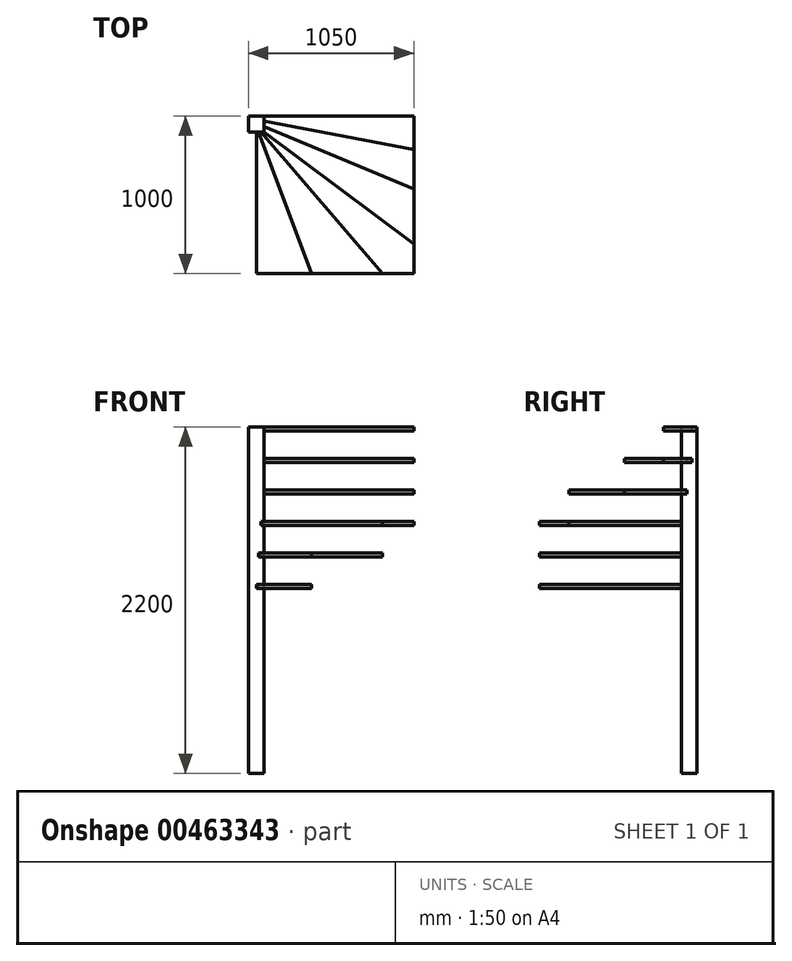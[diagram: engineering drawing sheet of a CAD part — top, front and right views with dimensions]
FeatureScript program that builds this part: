
annotation { "Feature Type Name" : "Feature", "Feature Type Description" : "" }
export const myFeature = defineFeature(function(context is Context, id is Id, definition is map)
    precondition{}
    {
        {
            var Q0;
            Q0=qCreatedBy(makeId("Top.planeOp"),FACE);
            var sketch = newSketch(context, id + "F0", { "sketchPlane" : qUnion([Q0])});
            skLineSegment(sketch, "E0.bottom", {"start": v(-50, 50) * mm, "end": v(50, 50) * mm});
            skLineSegment(sketch, "E0.top", {"start": v(-50, -50) * mm, "end": v(50, -50) * mm});
            skLineSegment(sketch, "E0.left", {"start": v(-50, 50) * mm, "end": v(-50, -50) * mm});
            skLineSegment(sketch, "E0.right", {"start": v(50, 50) * mm, "end": v(50, -50) * mm});
            skPoint(sketch, "E0.middle", {"position": v(0, 0) * mm});
            skSolve(sketch);
        }
        {
            var Q0;
            Q0=makeQuery(id+"F0.imprint","IMPRINT",FACE,{"disambiguationData":[TD([[makeQuery(id+"F0.imprint","IMPRINT",EDGE,{"derivedFrom":sQuery(id+"F0.wireOp",EDGE,"E0.bottom")}),-1.0]])]});
            extrude(context, id + "F1", {"entities" : qUnion([Q0]), "oppositeDirection" : true, "depth" : 2200 * mm, "offsetDistance" : 25 * mm});
        }
        {
            var Q0;
            Q0=makeQuery(id+"F1.opExtrude","CAP_FACE",FACE,{"disambiguationData":[OSD([sQuery(id+"F0.wireOp",EDGE,"E0.bottom"),sQuery(id+"F0.wireOp",EDGE,"E0.top"),sQuery(id+"F0.wireOp",EDGE,"E0.left"),sQuery(id+"F0.wireOp",EDGE,"E0.right")])],"isStart":true});
            var sketch = newSketch(context, id + "F2", { "sketchPlane" : qUnion([Q0])});
            skLineSegment(sketch, "E1", {"start": v(50, 50) * mm, "end": v(1000, 50) * mm});
            skLineSegment(sketch, "E2", {"start": v(1000, 50) * mm, "end": v(1000, -163.05) * mm});
            skLineSegment(sketch, "E3", {"start": v(1000, -163.05) * mm, "end": v(50, 17) * mm});
            skLineSegment(sketch, "E4", {"start": v(50, 17) * mm, "end": v(50, 50) * mm});
            skSolve(sketch);
        }
        {
            var Q0;
            Q0=makeQuery(id+"F2.imprint","IMPRINT",FACE,{"disambiguationData":[TD([[makeQuery(id+"F2.imprint","IMPRINT",EDGE,{"derivedFrom":sQuery(id+"F2.wireOp",EDGE,"E1")}),-1.0]])]});
            extrude(context, id + "F3", {"entities" : qUnion([Q0]), "oppositeDirection" : true, "depth" : 25 * mm, "offsetDistance" : 25 * mm});
        }
        {
            var Q0;
            Q0=qCreatedBy(makeId("Top.planeOp"),FACE);
            var sketch = newSketch(context, id + "F4", { "sketchPlane" : qUnion([Q0])});
            skLineSegment(sketch, "E5.0", {"start": v(50, 50) * mm, "end": v(1000, 50) * mm});
            skLineSegment(sketch, "E6.0", {"start": v(1000, 50) * mm, "end": v(1000, -163.05) * mm});
            skLineSegment(sketch, "E7.bottom", {"start": v(1000, 50) * mm, "end": v(-1000, 50) * mm});
            skLineSegment(sketch, "E7.top", {"start": v(1000, -950) * mm, "end": v(-1000, -950) * mm});
            skLineSegment(sketch, "E7.left", {"start": v(1000, 50) * mm, "end": v(1000, -950) * mm});
            skLineSegment(sketch, "E7.right", {"start": v(-1000, 50) * mm, "end": v(-1000, -950) * mm});
            skSolve(sketch);
        }
        {
            var Q0;
            Q0=makeQuery(id+"F1.opExtrude","CAP_FACE",FACE,{"disambiguationData":[OSD([sQuery(id+"F0.wireOp",EDGE,"E0.bottom"),sQuery(id+"F0.wireOp",EDGE,"E0.top"),sQuery(id+"F0.wireOp",EDGE,"E0.left"),sQuery(id+"F0.wireOp",EDGE,"E0.right")])],"isStart":true});
            cPlane(context, id + "F5", {"entities" : qUnion([Q0]), "cplaneType" : CPlaneType.OFFSET, "offset" : 200 * mm, "oppositeDirection" : true, "width" : 150 * mm, "height" : 150 * mm});
        }
        {
            var Q0;
            Q0=qCreatedBy(id+"F5.planeOp",FACE);
            cPlane(context, id + "F6", {"entities" : qUnion([Q0]), "cplaneType" : CPlaneType.OFFSET, "offset" : 200 * mm, "oppositeDirection" : true, "width" : 150 * mm, "height" : 150 * mm});
        }
        {
            var Q0;
            Q0=qCreatedBy(id+"F6.planeOp",FACE);
            cPlane(context, id + "F7", {"entities" : qUnion([Q0]), "cplaneType" : CPlaneType.OFFSET, "offset" : 200 * mm, "oppositeDirection" : true, "width" : 150 * mm, "height" : 150 * mm});
        }
        {
            var Q0;
            Q0=qCreatedBy(id+"F7.planeOp",FACE);
            cPlane(context, id + "F8", {"entities" : qUnion([Q0]), "cplaneType" : CPlaneType.OFFSET, "offset" : 200 * mm, "oppositeDirection" : true, "width" : 150 * mm, "height" : 150 * mm});
        }
        {
            var Q0;
            Q0=qCreatedBy(id+"F8.planeOp",FACE);
            cPlane(context, id + "F9", {"entities" : qUnion([Q0]), "cplaneType" : CPlaneType.OFFSET, "offset" : 200 * mm, "oppositeDirection" : true, "width" : 150 * mm, "height" : 150 * mm});
        }
        {
            var Q0;
            Q0=qCreatedBy(id+"F9.planeOp",FACE);
            cPlane(context, id + "F10", {"entities" : qUnion([Q0]), "cplaneType" : CPlaneType.OFFSET, "offset" : 200 * mm, "oppositeDirection" : true, "width" : 150 * mm, "height" : 150 * mm});
        }
        {
            var Q0;
            Q0=qCreatedBy(id+"F10.planeOp",FACE);
            cPlane(context, id + "F11", {"entities" : qUnion([Q0]), "cplaneType" : CPlaneType.OFFSET, "offset" : 200 * mm, "oppositeDirection" : true, "width" : 150 * mm, "height" : 150 * mm});
        }
        {
            var Q0;
            Q0=qCreatedBy(id+"F11.planeOp",FACE);
            cPlane(context, id + "F12", {"entities" : qUnion([Q0]), "cplaneType" : CPlaneType.OFFSET, "offset" : 200 * mm, "oppositeDirection" : true, "width" : 150 * mm, "height" : 150 * mm});
        }
        {
            var Q0;
            Q0=qCreatedBy(id+"F12.planeOp",FACE);
            cPlane(context, id + "F13", {"entities" : qUnion([Q0]), "cplaneType" : CPlaneType.OFFSET, "offset" : 200 * mm, "oppositeDirection" : true, "width" : 150 * mm, "height" : 150 * mm});
        }
        {
            var Q0;
            Q0=qCreatedBy(id+"F5.planeOp",FACE);
            var sketch = newSketch(context, id + "F14", { "sketchPlane" : qUnion([Q0])});
            skLineSegment(sketch, "E8.0", {"start": v(1000, -163.05) * mm, "end": v(50, 17) * mm});
            skLineSegment(sketch, "E9.0", {"start": v(50, 17) * mm, "end": v(50, -16) * mm});
            skLineSegment(sketch, "E10", {"start": v(50, -16) * mm, "end": v(1000, -413.05) * mm});
            skLineSegment(sketch, "E11", {"start": v(1000, -413.05) * mm, "end": v(1000, -163.05) * mm});
            skPoint(sketch, "E12.orphan", {"position": v(50, 50) * mm});
            skPoint(sketch, "E13.orphan", {"position": v(50, -50) * mm});
            skSolve(sketch);
        }
        {
            var Q0;
            Q0=qCreatedBy(id+"F6.planeOp",FACE);
            var sketch = newSketch(context, id + "F15", { "sketchPlane" : qUnion([Q0])});
            skLineSegment(sketch, "E14.0", {"start": v(50, -16) * mm, "end": v(1000, -413.05) * mm});
            skLineSegment(sketch, "E15.0", {"start": v(50, -16) * mm, "end": v(50, -50) * mm});
            skLineSegment(sketch, "E16", {"start": v(50, -50) * mm, "end": v(1000, -763.05) * mm});
            skLineSegment(sketch, "E17", {"start": v(1000, -763.05) * mm, "end": v(1000, -413.05) * mm});
            skPoint(sketch, "E18.orphan", {"position": v(50, 50) * mm});
            skSolve(sketch);
        }
        {
            var Q0;
            Q0=qCreatedBy(id+"F7.planeOp",FACE);
            var sketch = newSketch(context, id + "F16", { "sketchPlane" : qUnion([Q0])});
            skLineSegment(sketch, "E19.0", {"start": v(50, -50) * mm, "end": v(1000, -763.05) * mm});
            skLineSegment(sketch, "E20.0", {"start": v(30, -50) * mm, "end": v(50, -50) * mm});
            skLineSegment(sketch, "E21.0", {"start": v(1000, -950) * mm, "end": v(800, -950) * mm});
            skLineSegment(sketch, "E22.0", {"start": v(1000, -763.05) * mm, "end": v(1000, -950) * mm});
            skLineSegment(sketch, "E23", {"start": v(30, -50) * mm, "end": v(800, -950) * mm});
            skPoint(sketch, "E24.orphan", {"position": v(-50, -50) * mm});
            skPoint(sketch, "E25.orphan", {"position": v(1000, 50) * mm});
            skPoint(sketch, "E26.orphan", {"position": v(-1000, -950) * mm});
            skSolve(sketch);
        }
        {
            var Q0;
            Q0=qCreatedBy(id+"F8.planeOp",FACE);
            var sketch = newSketch(context, id + "F17", { "sketchPlane" : qUnion([Q0])});
            skLineSegment(sketch, "E27.0", {"start": v(15, -50) * mm, "end": v(50, -50) * mm});
            skLineSegment(sketch, "E28.0", {"start": v(30, -50) * mm, "end": v(800, -950) * mm});
            skLineSegment(sketch, "E29.0", {"start": v(800, -950) * mm, "end": v(350, -950) * mm});
            skLineSegment(sketch, "E30", {"start": v(15, -50) * mm, "end": v(350, -950) * mm});
            skPoint(sketch, "E31.orphan", {"position": v(-1000, -950) * mm});
            skPoint(sketch, "E32.orphan", {"position": v(1000, -950) * mm});
            skPoint(sketch, "E33.orphan", {"position": v(-50, -50) * mm});
            skSolve(sketch);
        }
        {
            var Q0;
            Q0=qCreatedBy(id+"F9.planeOp",FACE);
            var sketch = newSketch(context, id + "F18", { "sketchPlane" : qUnion([Q0])});
            skLineSegment(sketch, "E34.0", {"start": v(0, -50) * mm, "end": v(15, -50) * mm});
            skLineSegment(sketch, "E35.0", {"start": v(15, -50) * mm, "end": v(350, -950) * mm});
            skLineSegment(sketch, "E36.0", {"start": v(350, -950) * mm, "end": v(0, -950) * mm});
            skLineSegment(sketch, "E37", {"start": v(0, -50) * mm, "end": v(0, -950) * mm});
            skPoint(sketch, "E38.orphan", {"position": v(-1000, -950) * mm});
            skPoint(sketch, "E39.orphan", {"position": v(1000, -950) * mm});
            skPoint(sketch, "E40.orphan", {"position": v(-50, -50) * mm});
            skPoint(sketch, "E41.orphan", {"position": v(50, -50) * mm});
            skSolve(sketch);
        }
        {
            var Q0;
            Q0=makeQuery(id+"F14.imprint","IMPRINT",FACE,{"disambiguationData":[TD([[makeQuery(id+"F14.imprint","IMPRINT",EDGE,{"derivedFrom":sQuery(id+"F14.wireOp",EDGE,"E8.0")}),1.0]])]});
            var Q1;
            Q1=makeQuery(id+"F15.imprint","IMPRINT",FACE,{"disambiguationData":[TD([[makeQuery(id+"F15.imprint","IMPRINT",EDGE,{"derivedFrom":sQuery(id+"F15.wireOp",EDGE,"E14.0")}),-1.0]])]});
            var Q2;
            Q2=makeQuery(id+"F16.imprint","IMPRINT",FACE,{"disambiguationData":[TD([[makeQuery(id+"F16.imprint","IMPRINT",EDGE,{"derivedFrom":sQuery(id+"F16.wireOp",EDGE,"E19.0")}),-1.0]])]});
            var Q3;
            {var subQ2=sQuery(id+"F17.wireOp",EDGE,"E28.0");Q3=makeQuery(id+"F17.imprint","IMPRINT",FACE,{"disambiguationData":[TD([[makeQuery(id+"F17.imprint","IMPRINT",EDGE,{"derivedFrom":subQ2}),-1.0]])]});}
            var Q4;
            Q4=makeQuery(id+"F18.imprint","IMPRINT",FACE,{"disambiguationData":[TD([[makeQuery(id+"F18.imprint","IMPRINT",EDGE,{"derivedFrom":sQuery(id+"F18.wireOp",EDGE,"E34.0")}),-1.0]])]});
            extrude(context, id + "F19", {"entities" : qUnion([Q0, Q1, Q2, Q3, Q4]), "operationType" : NewBodyOperationType.ADD, "oppositeDirection" : true, "depth" : 25 * mm, "offsetDistance" : 25 * mm});
        }
    });
